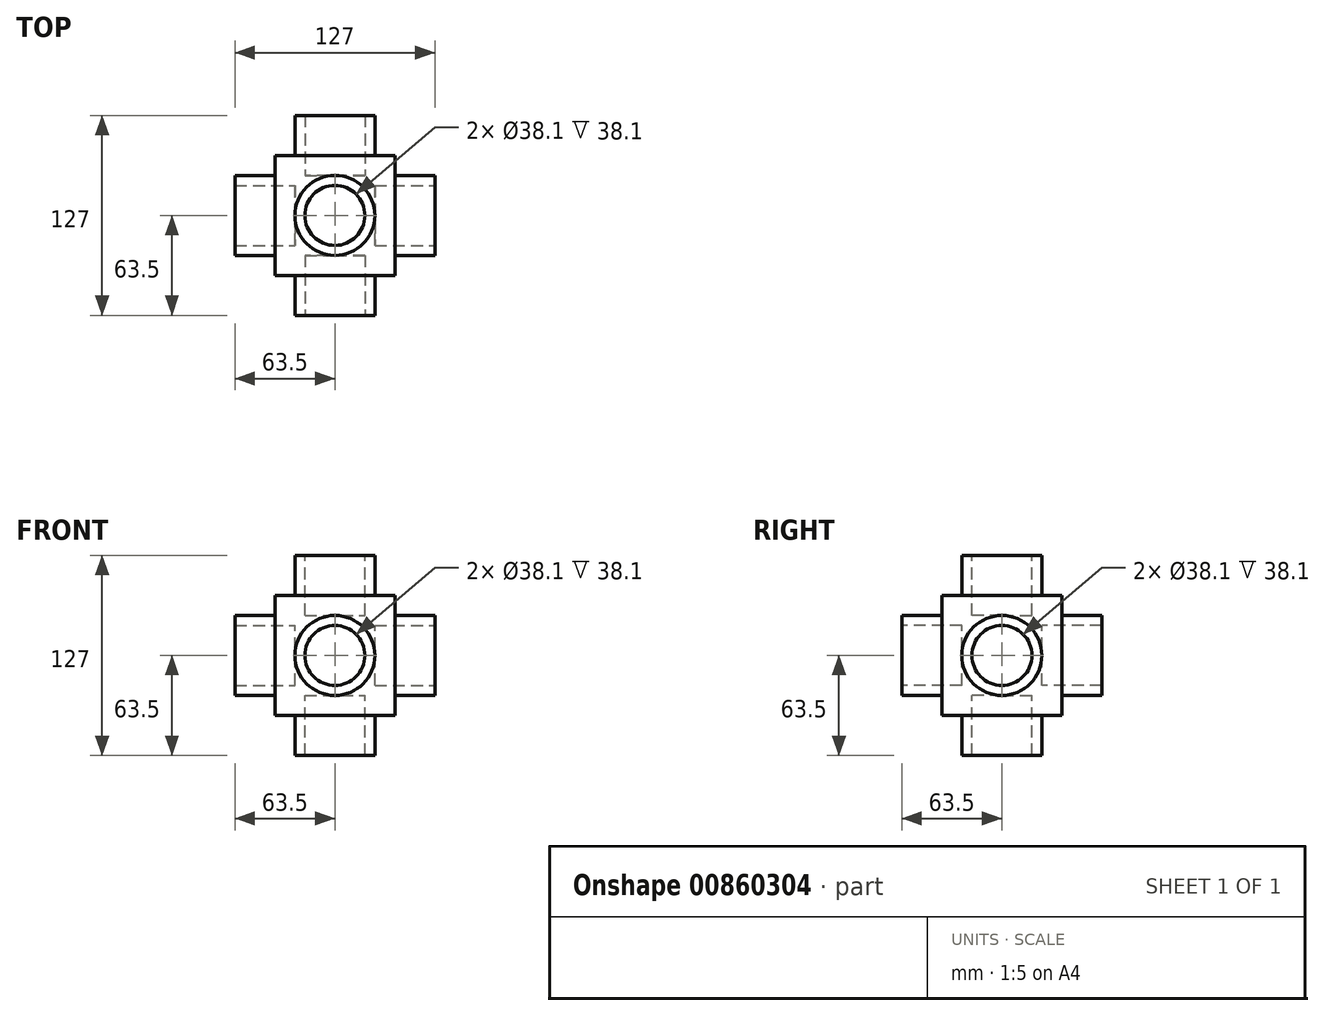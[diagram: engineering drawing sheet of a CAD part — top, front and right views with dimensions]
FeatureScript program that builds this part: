
annotation { "Feature Type Name" : "Feature", "Feature Type Description" : "" }
export const myFeature = defineFeature(function(context is Context, id is Id, definition is map)
    precondition{}
    {
        {
            var Q0;
            Q0=qCreatedBy(makeId("Top.planeOp"),FACE);
            var sketch = newSketch(context, id + "F0", { "sketchPlane" : qUnion([Q0])});
            skLineSegment(sketch, "E0.bottom", {"start": v(38.1, 38.1) * mm, "end": v(-38.1, 38.1) * mm});
            skLineSegment(sketch, "E0.top", {"start": v(38.1, -38.1) * mm, "end": v(-38.1, -38.1) * mm});
            skLineSegment(sketch, "E0.left", {"start": v(38.1, 38.1) * mm, "end": v(38.1, -38.1) * mm});
            skLineSegment(sketch, "E0.right", {"start": v(-38.1, 38.1) * mm, "end": v(-38.1, -38.1) * mm});
            skPoint(sketch, "E0.middle", {"position": v(0, 0) * mm});
            skCircle(sketch, "E1", {"center": v(0, 0) * mm, "radius": 25.4 * mm});
            skSolve(sketch);
        }
        {
            var Q0;
            Q0 = qSketchRegion(id + "F0", true);
            extrude(context, id + "F1", {"entities" : qUnion([Q0]), "endBound" : BoundingType.SYMMETRIC, "depth" : 76.2 * mm, "offsetDistance" : 25.4 * mm});
        }
        {
            var Q0;
            Q0=makeQuery(id+"F0.imprint","IMPRINT",FACE,{"disambiguationData":[TD([[makeQuery(id+"F0.imprint","IMPRINT",EDGE,{"derivedFrom":sQuery(id+"F0.wireOp",EDGE,"E1")}),1.0]])]});
            extrude(context, id + "F2", {"entities" : qUnion([Q0]), "operationType" : NewBodyOperationType.ADD, "endBound" : BoundingType.SYMMETRIC, "depth" : 127 * mm, "offsetDistance" : 25.4 * mm});
        }
        {
            var Q0;
            Q0=qCreatedBy(makeId("Front.planeOp"),FACE);
            var sketch = newSketch(context, id + "F3", { "sketchPlane" : qUnion([Q0])});
            skCircle(sketch, "E2", {"center": v(0, 0) * mm, "radius": 25.4 * mm});
            skSolve(sketch);
        }
        {
            var Q0;
            Q0 = qSketchRegion(id + "F3", true);
            extrude(context, id + "F4", {"entities" : qUnion([Q0]), "operationType" : NewBodyOperationType.ADD, "endBound" : BoundingType.SYMMETRIC, "depth" : 127 * mm, "offsetDistance" : 25.4 * mm});
        }
        {
            var Q0;
            Q0=qCreatedBy(makeId("Right.planeOp"),FACE);
            var sketch = newSketch(context, id + "F5", { "sketchPlane" : qUnion([Q0])});
            skCircle(sketch, "E3", {"center": v(0, 0) * mm, "radius": 25.4 * mm});
            skSolve(sketch);
        }
        {
            var Q0;
            Q0 = qSketchRegion(id + "F5", true);
            extrude(context, id + "F6", {"entities" : qUnion([Q0]), "operationType" : NewBodyOperationType.ADD, "endBound" : BoundingType.SYMMETRIC, "depth" : 127 * mm, "offsetDistance" : 25.4 * mm});
        }
        {
            var Q0;
            Q0=makeQuery(id+"F2.opExtrude","CAP_FACE",FACE,{"disambiguationData":[OSD([sQuery(id+"F0.wireOp",EDGE,"E1")])],"isStart":false});
            var sketch = newSketch(context, id + "F7", { "sketchPlane" : qUnion([Q0])});
            skCircle(sketch, "E4", {"center": v(0, 0) * mm, "radius": 19.05 * mm});
            skSolve(sketch);
        }
        {
            var Q0;
            Q0 = qSketchRegion(id + "F7", true);
            extrude(context, id + "F8", {"entities" : qUnion([Q0]), "operationType" : NewBodyOperationType.REMOVE, "endBound" : BoundingType.THROUGH_ALL, "oppositeDirection" : true, "depth" : 25.4 * mm, "offsetDistance" : 25.4 * mm});
        }
        {
            var Q0;
            Q0=makeQuery(id+"F4.opExtrude","CAP_FACE",FACE,{"disambiguationData":[OSD([sQuery(id+"F3.wireOp",EDGE,"E2")])],"isStart":false});
            var sketch = newSketch(context, id + "F9", { "sketchPlane" : qUnion([Q0])});
            skCircle(sketch, "E5", {"center": v(0, 0) * mm, "radius": 19.05 * mm});
            skSolve(sketch);
        }
        {
            var Q0;
            Q0 = qSketchRegion(id + "F9", true);
            extrude(context, id + "F10", {"entities" : qUnion([Q0]), "operationType" : NewBodyOperationType.REMOVE, "endBound" : BoundingType.THROUGH_ALL, "oppositeDirection" : true, "depth" : 25.4 * mm, "offsetDistance" : 25.4 * mm});
        }
        {
            var Q0;
            Q0=makeQuery(id+"F6.opExtrude","CAP_FACE",FACE,{"disambiguationData":[OSD([sQuery(id+"F5.wireOp",EDGE,"E3")])],"isStart":false});
            var sketch = newSketch(context, id + "F11", { "sketchPlane" : qUnion([Q0])});
            skCircle(sketch, "E6", {"center": v(0, 0) * mm, "radius": 19.05 * mm});
            skSolve(sketch);
        }
        {
            var Q0;
            Q0 = qSketchRegion(id + "F11", true);
            extrude(context, id + "F12", {"entities" : qUnion([Q0]), "operationType" : NewBodyOperationType.REMOVE, "endBound" : BoundingType.THROUGH_ALL, "oppositeDirection" : true, "depth" : 25.4 * mm, "offsetDistance" : 25.4 * mm});
        }
        {
            var Q0;
            Q0=qCreatedBy(makeId("Front.planeOp"),FACE);
            var sketch = newSketch(context, id + "F13", { "sketchPlane" : qUnion([Q0])});
            skLineSegment(sketch, "E7.bottom", {"start": v(25.4, 25.4) * mm, "end": v(-25.4, 25.4) * mm});
            skLineSegment(sketch, "E7.top", {"start": v(25.4, -25.4) * mm, "end": v(-25.4, -25.4) * mm});
            skLineSegment(sketch, "E7.left", {"start": v(25.4, 25.4) * mm, "end": v(25.4, -25.4) * mm});
            skLineSegment(sketch, "E7.right", {"start": v(-25.4, 25.4) * mm, "end": v(-25.4, -25.4) * mm});
            skPoint(sketch, "E7.middle", {"position": v(0, 0) * mm});
            skSolve(sketch);
        }
        {
            var Q0;
            Q0 = qSketchRegion(id + "F13", true);
            extrude(context, id + "F14", {"entities" : qUnion([Q0]), "operationType" : NewBodyOperationType.ADD, "endBound" : BoundingType.SYMMETRIC, "depth" : 50.8 * mm, "offsetDistance" : 25.4 * mm});
        }
    });
